# Revit family: BISLEY_Note_Pedestals
name_source: partatom
category: Furniture
revit_build: Autodesk Revit 2018 (Build: 20180423_1000(x64)
units: mm (PartAtom-declared; Revit-internal decimal feet)

## family parameters
Always vertical = Yes
Cut with Voids When Loaded = No
OmniClass Number = 23.40.20.00
OmniClass Title = General Furniture and Specialties
Room Calculation Point = No
Shared = No
Work Plane-Based = No

## types (14) — shared parameters
AssetType = Moveable
BIMObjectName = NBS_Bisley_OfficeFittingsFurnishingsAndEquipmentSystem_NotePedestal
Category = Pedestals
Color = Available in 16 finishes. For more info call: 020 7436 7111
Depth = 565 mm  [stored 1.85367 ft]
Description = Castor based or static under-desk pedestal.
Door width = 210 mm  [stored 0.688976 ft]
ExpectedLife = 5-10
Features = Robust welded steel carcase, Anti-tilt mechanism, 100% extension file drawers, Optional drop-in pen tray, 6mm decorative top-optional
Finish = Powder coated, available in 16 colours
Freestanding top = Yes
Manufacturer = Bisley Office Furniture
ManufacturerName = Bisley Office Furniture
ManufacturerURL = http://www.bisley.com
Material = Steel
Model = Note Pedestal
ModelReference = Note Pedestal
Name = OfficeFittingsFurnishingsAndEquipmentSystem_NotePedestal_Bisley
ReplacementCost = Please contact us on 01633 637 383 or http://www.bisley.com
Shape = Box
SustainabilityPerformance = BS EN 14073 2004 Part 2 & 3, BS EN 14074 2004, BS 4875 1998 Part 7 level 4 & Part 8, DIN 4554/485
URL = http://www.bisley.com
Uniclass 2015 Code = PR_40_30_25
Uniclass2015Title = Shelves and Storage Units
Uniclass2015Version = V1.1
WarrantyDescription = The product is used during normal office hours
WarrantyDurationLabor = 5
WarrantyDurationParts = 5
WarrantyDurationUnit = year
WarrantyGuarantorLabor = Bisley
WarrantyGuarantorParts = Bisley
WarrantyStartDate = Date of purchase
extra depth = Yes
plinth height = 40 mm  [stored 0.131234 ft]
top = Yes

## per-type parameters (varying)
| type | 20 | 2nd Drawer height | 3rd Drawer height | 3rd drawer | Bottom Door height | Castor | Height | Lock height | ModelNumber | Size | Width | back height | back panels | top depth | top piece |
| NWA59M7SF | 0 mm  [stored 0 ft] | 153 mm  [stored 0.501969 ft] | 101 mm | No | 300 mm | Yes | 495 mm  [stored 1.62402 ft] | 380 mm | NWA59M7SF | 420 x 565 x 495 mm, Packed: 440 x 640 x 500 mm | 420 mm  [stored 1.37795 ft] | 495 mm  [stored 1.62402 ft] | 0 mm  [stored 0 ft] | 61 mm | 43 mm |
| NWA59M7SSS | 0 mm  [stored 0 ft] | 150 mm | 150 mm | Yes | 150 mm | No | 495 mm  [stored 1.62402 ft] | 380 mm | NWA59M7SSS | 420 x 565 x 495 mm, Packed: 440 x 640 x 500 mm | 420 mm  [stored 1.37795 ft] | 495 mm  [stored 1.62402 ft] | 0 mm  [stored 0 ft] | 61 mm | 43 mm |
| NWA5AM7IIF | 0 mm  [stored 0 ft] | 111 mm | 111 mm | Yes | 300 mm | Yes | 567 mm  [stored 1.86024 ft] | 470 mm  [stored 1.54199 ft] | NWA5AM7IIF | 420 x 565 x 567 mm, Packed: 440 x 640 x 570 mm | 420 mm  [stored 1.37795 ft] | 567 mm  [stored 1.86024 ft] | 0 mm  [stored 0 ft] | 61 mm | 43 mm |
| NWA52M7SSF | 0 mm  [stored 0 ft] | 150 mm | 150 mm | Yes | 300 mm | Yes | 645 mm  [stored 2.11614 ft] | 525 mm | NWA52M7SSF | 420 x 565 x 645 mm, Pacekd: 440 x 640 x 650 mm | 420 mm  [stored 1.37795 ft] | 645 mm  [stored 2.11614 ft] | 0 mm  [stored 0 ft] | 61 mm | 43 mm |
| NWA52M7FF | 0 mm  [stored 0 ft] | 300 mm | 150 mm | No | 300 mm | No | 645 mm  [stored 2.11614 ft] | 362 mm  [stored 1.18766 ft] | NWA52M7FF | 420 x 565 x 645 mm, Pacekd: 440 x 640 x 650 mm | 420 mm  [stored 1.37795 ft] | 645 mm  [stored 2.11614 ft] | 0 mm  [stored 0 ft] | 61 mm | 43 mm |
| NW359M7SF | 0 mm  [stored 0 ft] | 153 mm  [stored 0.501969 ft] | 101 mm | No | 300 mm | Yes | 495 mm  [stored 1.62402 ft] | 380 mm | NW359M7SF | 300 x 565 x 495 mm, Packed: 330 x 640 x 500 mm | 300 mm | 495 mm  [stored 1.62402 ft] | 0 mm  [stored 0 ft] | 61 mm | 43 mm |
| NW359M7SSS | 0 mm  [stored 0 ft] | 150 mm | 150 mm | Yes | 150 mm | No | 495 mm  [stored 1.62402 ft] | 380 mm | NW359M7SSS | 300 x 565 x 495 mm, Packed: 330 x 640 x 500 mm | 300 mm | 495 mm  [stored 1.62402 ft] | 0 mm  [stored 0 ft] | 61 mm | 43 mm |
| NW35AM7IIF | 0 mm  [stored 0 ft] | 111 mm | 111 mm | Yes | 300 mm | Yes | 567 mm  [stored 1.86024 ft] | 470 mm  [stored 1.54199 ft] | NW35AM7IIF | 300 x 565 x 567 mm | 300 mm | 567 mm  [stored 1.86024 ft] | 0 mm  [stored 0 ft] | 61 mm | 43 mm |
| NW352M7FF | 0 mm  [stored 0 ft] | 300 mm | 150 mm | No | 300 mm | No | 645 mm  [stored 2.11614 ft] | 362 mm  [stored 1.18766 ft] | NW352M7FF | 300 x 565 x 645 mm, Packed: 330 x 640 x 650 mm | 300 mm | 645 mm  [stored 2.11614 ft] | 0 mm  [stored 0 ft] | 61 mm | 43 mm |
| NW352M7SSF | 0 mm  [stored 0 ft] | 150 mm | 150 mm | Yes | 300 mm | Yes | 645 mm  [stored 2.11614 ft] | 525 mm | NW352M7SSF | 300 x 565 x 645 mm, Packed:330 x 640 x 650 mm | 300 mm | 645 mm  [stored 2.11614 ft] | 0 mm  [stored 0 ft] | 61 mm | 43 mm |
| NWA53G7FF | 21 mm  [stored 0.0688976 ft] | 300 mm | 150 mm | No | 300 mm | No | 698 mm  [stored 2.29003 ft] | 362 mm  [stored 1.18766 ft] | NWA53G7FF | 420 x 565 x 698 mm, Packed: 440 x 640 x 710 mm | 420 mm  [stored 1.37795 ft] | 698 mm  [stored 2.29003 ft] | 0 mm  [stored 0 ft] | 61 mm | 54 mm  [stored 0.177165 ft] |
| NWA53G7SSF | 21 mm  [stored 0.0688976 ft] | 150 mm | 150 mm | Yes | 300 mm | Yes | 698 mm  [stored 2.29003 ft] | 525 mm | NWA53G7SSF | 420 x 565 x 698 mm, Pacekd: 440 x 640 x 710 mm | 420 mm  [stored 1.37795 ft] | 698 mm  [stored 2.29003 ft] | 0 mm  [stored 0 ft] | 61 mm | 53 mm  [stored 0.173885 ft] |
| NWA73G7FF | 21 mm  [stored 0.0688976 ft] | 300 mm | 150 mm | No | 300 mm | No | 698 mm  [stored 2.29003 ft] | 362 mm  [stored 1.18766 ft] | NWA52M7FF | 420 x 775 x 698 mm, Pacekd: 440 x 850 x 710 mm | 420 mm  [stored 1.37795 ft] | 698 mm  [stored 2.29003 ft] | 190 mm | 61 mm | 54 mm  [stored 0.177165 ft] |
| NWA73G7SSF | 20 mm  [stored 0.0656168 ft] | 150 mm | 150 mm | Yes | 300 mm | Yes | 698 mm  [stored 2.29003 ft] | 525 mm | NWA52M7SSF | 420 x 775 x 698 mm, Pacekd: 440 x 850 x 710 mm | 420 mm  [stored 1.37795 ft] | 698 mm  [stored 2.29003 ft] | 190 mm | 20 mm  [stored 0.0656168 ft] | 53 mm  [stored 0.173885 ft] |

note: [stored X ft] marks values corroborated as IEEE doubles in the binary element streams (Revit-internal decimal feet)

## geometry (parser evidence)
native form markers: Sweep x2
no freeform markers — native parametric forms only
